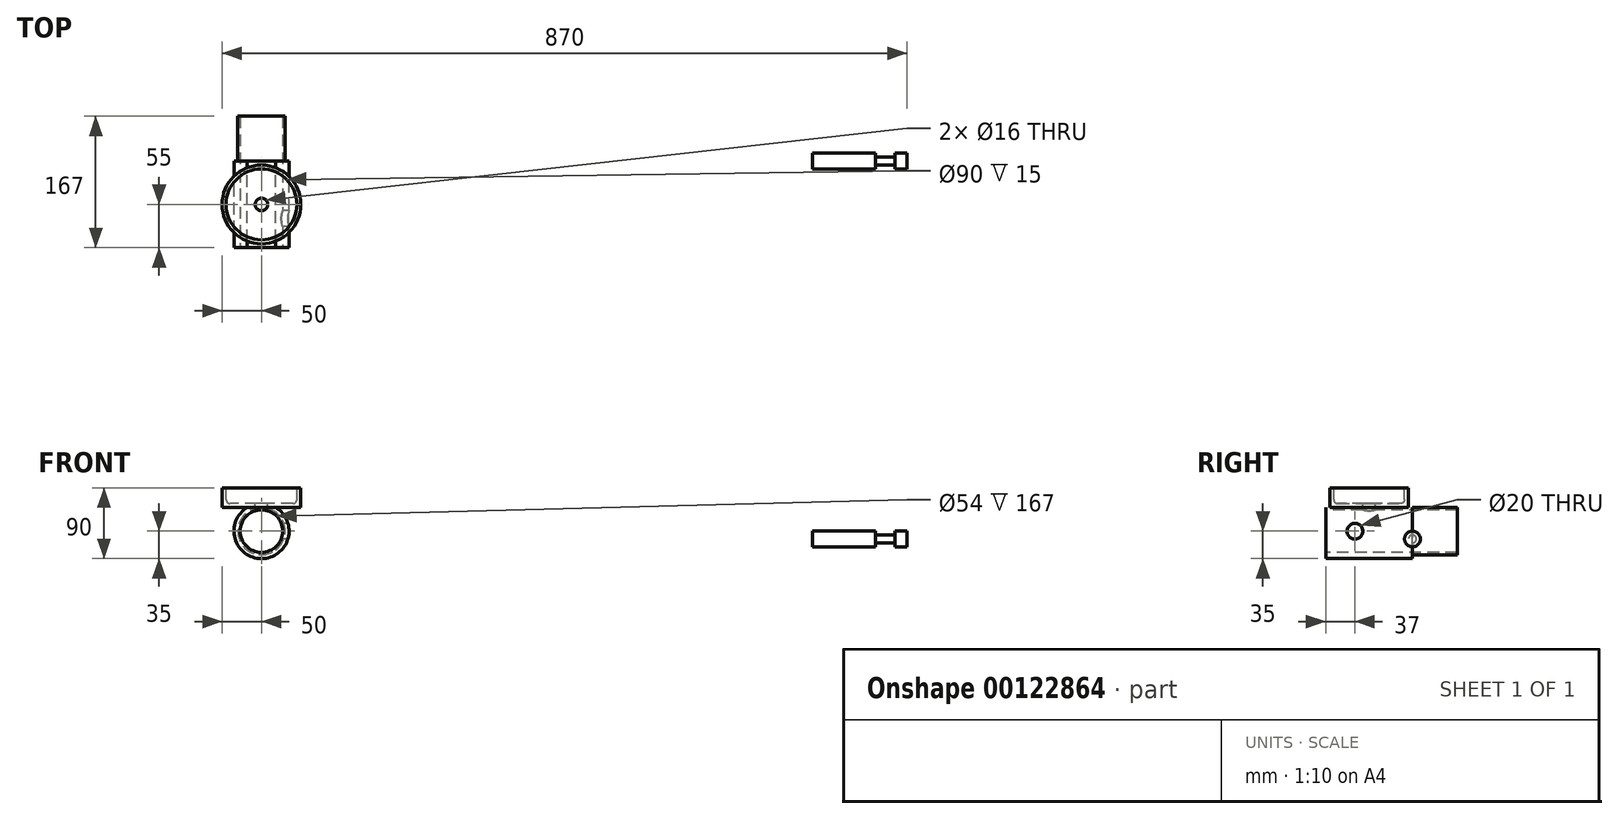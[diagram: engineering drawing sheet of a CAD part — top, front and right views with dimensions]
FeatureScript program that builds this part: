
annotation { "Feature Type Name" : "Feature", "Feature Type Description" : "" }
export const myFeature = defineFeature(function(context is Context, id is Id, definition is map)
    precondition{}
    {
        {
            var Q0;
            Q0=qCreatedBy(makeId("Front.planeOp"),FACE);
            var sketch = newSketch(context, id + "F0", { "sketchPlane" : qUnion([Q0])});
            skArc(sketch, "E0", {"start": v(-16.66, -30.78) * mm, "mid": v(35, 0) * mm, "end": v(-16.66, 30.78) * mm});
            skArc(sketch, "E1", {"start": v(-618.13, 87.33) * mm, "mid": v(-673.03, 71.59) * mm, "end": v(-640, 25) * mm});
            skCircle(sketch, "E2", {"center": v(-700, 0) * mm, "radius": 27.5 * mm, "construction": true});
            skCircle(sketch, "E3", {"center": v(-640, 60) * mm, "radius": 26.5 * mm});
            skCircle(sketch, "E4", {"center": v(-640, -60) * mm, "radius": 26.5 * mm});
            skCircle(sketch, "E5", {"center": v(0, 0) * mm, "radius": 26.5 * mm});
            skLineSegment(sketch, "E6", {"start": v(-40.48, 24.76) * mm, "end": v(-475.65, 24.99) * mm});
            skLineSegment(sketch, "E7", {"start": v(-40.48, -24.76) * mm, "end": v(-475.65, -24.99) * mm});
            skLineSegment(sketch, "E8", {"start": v(-521.62, -36.2) * mm, "end": v(-609.9, -81.98) * mm});
            skLineSegment(sketch, "E9", {"start": v(-521.62, 36.2) * mm, "end": v(-609.9, 81.98) * mm});
            skPoint(sketch, "E10.visualSharp", {"position": v(-500, 25) * mm});
            skArc(sketch, "E10.filletArc", {"start": v(-521.62, 36.2) * mm, "mid": v(-499.3, 27.84) * mm, "end": v(-475.65, 24.99) * mm});
            skPoint(sketch, "E11.visualSharp", {"position": v(-500, -25) * mm});
            skArc(sketch, "E11.filletArc", {"start": v(-475.65, -24.99) * mm, "mid": v(-499.3, -27.84) * mm, "end": v(-521.62, -36.2) * mm});
            skPoint(sketch, "E12.visualSharp", {"position": v(-615.25, 84.75) * mm});
            skArc(sketch, "E13", {"start": v(-640, -25) * mm, "mid": v(-673.03, -71.59) * mm, "end": v(-618.13, -87.33) * mm});
            skFitSpline(sketch, "E14", {"points": [v(-640, -25) * mm, v(-580, 0) * mm, v(-640, 25) * mm], "startDerivative": vector(150, -30) * mm, "endDerivative": vector(-150, -30) * mm});
            skPoint(sketch, "E15.visualSharp", {"position": v(-615.25, -84.75) * mm});
            skLineSegment(sketch, "E16", {"start": v(-24.75, 24.75) * mm, "end": v(0, 0) * mm, "construction": true});
            skLineSegment(sketch, "E17", {"start": v(-24.75, -24.75) * mm, "end": v(0, 0) * mm, "construction": true});
            skPoint(sketch, "E18.visualSharp", {"position": v(-24.75, 24.75) * mm});
            skArc(sketch, "E18.filletArc", {"start": v(-40.48, 24.76) * mm, "mid": v(-28.2, 26.28) * mm, "end": v(-16.66, 30.78) * mm});
            skPoint(sketch, "E19.visualSharp", {"position": v(-24.75, -24.75) * mm});
            skArc(sketch, "E19.filletArc", {"start": v(-16.66, -30.78) * mm, "mid": v(-28.2, -26.28) * mm, "end": v(-40.48, -24.76) * mm});
            skLineSegment(sketch, "E20", {"start": v(-615.25, 84.75) * mm, "end": v(-640, 60) * mm, "construction": true});
            skLineSegment(sketch, "E21", {"start": v(-640, -60) * mm, "end": v(-640, 177.49) * mm, "construction": true});
            skArc(sketch, "E22.filletArc", {"start": v(-618.13, 87.33) * mm, "mid": v(-614.15, 84.45) * mm, "end": v(-609.9, 81.98) * mm});
            skLineSegment(sketch, "E23", {"start": v(-615.25, -84.75) * mm, "end": v(-640, -60) * mm, "construction": true});
            skArc(sketch, "E24.filletArc", {"start": v(-609.9, -81.98) * mm, "mid": v(-614.15, -84.45) * mm, "end": v(-618.13, -87.33) * mm});
            skSolve(sketch);
        }
        {
            var Q0;
            Q0=qSketchRegion(id+"F0",true);
            extrude(context, id + "F1", {"entities" : qUnion([Q0]), "depth" : 45 * mm});
        }
        {
            var Q0;
            Q0=makeQuery(id+"F1.opExtrude","SWEPT_BODY",BODY,{"disambiguationData":[OSD([sQuery(id+"F0.wireOp",EDGE,"E0"),sQuery(id+"F0.wireOp",EDGE,"E1"),sQuery(id+"F0.wireOp",EDGE,"hKVllitM-rUlu-PjKN-B9u5-COeOs3Kio4uB"),sQuery(id+"F0.wireOp",EDGE,"bIEpRebq-8nbQ-7rQF-Jdrm-i3E8cfRsBNN9"),sQuery(id+"F0.wireOp",EDGE,"ymSRshFr-buK2-GFJu-27zL-H9ECYoIg19t0"),sQuery(id+"F0.wireOp",EDGE,"e6450e41-44a2-4cb5-af14-4686bec827bc"),sQuery(id+"F0.wireOp",EDGE,"ipdW7DlG-pZfv-p4Vr-qYAQ-uRQYnpMPVyQN"),sQuery(id+"F0.wireOp",EDGE,"9qNpO7d9-6r7V-397W-DIXA-CVevZtzhY8f4"),sQuery(id+"F0.wireOp",EDGE,"E3"),sQuery(id+"F0.wireOp",EDGE,"E4"),sQuery(id+"F0.wireOp",EDGE,"E5")])]});
            var Q1;
            Q1=makeQuery(id+"F1.opExtrude","CAP_EDGE",EDGE,{"disambiguationData":[OSD([sQuery(id+"F0.wireOp",EDGE,"E5")])],"isStart":false});
            transform(context, id + "F2", {"entities" : qUnion([Q0]), "transformType" : TransformType.ROTATION, "transformAxis" : qUnion([Q1]), "angle" : 12.5 * degree, "makeCopy" : true});
        }
        {
            var Q0;
            Q0=makeQuery(id+"F1.opExtrude","CAP_FACE",FACE,{"disambiguationData":[OSD([sQuery(id+"F0.wireOp",EDGE,"E0"),sQuery(id+"F0.wireOp",EDGE,"E1"),sQuery(id+"F0.wireOp",EDGE,"E3"),sQuery(id+"F0.wireOp",EDGE,"E4"),sQuery(id+"F0.wireOp",EDGE,"E5"),sQuery(id+"F0.wireOp",EDGE,"E6"),sQuery(id+"F0.wireOp",EDGE,"E7"),sQuery(id+"F0.wireOp",EDGE,"E8"),sQuery(id+"F0.wireOp",EDGE,"E9"),sQuery(id+"F0.wireOp",EDGE,"E10.filletArc"),sQuery(id+"F0.wireOp",EDGE,"E11.filletArc"),sQuery(id+"F0.wireOp",EDGE,"E13"),sQuery(id+"F0.wireOp",EDGE,"E14"),sQuery(id+"F0.wireOp",EDGE,"E18.filletArc"),sQuery(id+"F0.wireOp",EDGE,"E19.filletArc"),sQuery(id+"F0.wireOp",EDGE,"E22.filletArc"),sQuery(id+"F0.wireOp",EDGE,"E24.filletArc")])],"isStart":false});
            var sketch = newSketch(context, id + "F3", { "sketchPlane" : qUnion([Q0])});
            skLineSegment(sketch, "E25", {"start": v(-41.5, 14.76) * mm, "end": v(-502.44, 15) * mm});
            skLineSegment(sketch, "E26", {"start": v(-41.5, -14.76) * mm, "end": v(-502.44, -15) * mm});
            skLineSegment(sketch, "E27", {"start": v(-502.44, -15) * mm, "end": v(-592.4, -61.64) * mm});
            skLineSegment(sketch, "E28", {"start": v(-592.4, -61.64) * mm, "end": v(-606.21, -35) * mm});
            skLineSegment(sketch, "E29", {"start": v(-606.21, -35) * mm, "end": v(-564.37, -13.32) * mm});
            skLineSegment(sketch, "E30", {"start": v(-502.44, 15) * mm, "end": v(-592.4, 61.64) * mm});
            skLineSegment(sketch, "E31", {"start": v(-592.4, 61.64) * mm, "end": v(-606.21, 35) * mm});
            skLineSegment(sketch, "E32", {"start": v(-606.21, 35) * mm, "end": v(-564.37, 13.32) * mm});
            skPoint(sketch, "E33.visualSharp", {"position": v(-538.69, 0) * mm});
            skArc(sketch, "E33.filletArc", {"start": v(-564.37, -13.32) * mm, "mid": v(-556.28, 0) * mm, "end": v(-564.37, 13.32) * mm});
            skLineSegment(sketch, "E34", {"start": v(-41.5, 14.76) * mm, "end": v(-41.5, -14.76) * mm});
            skSolve(sketch);
        }
        {
            var Q0;
            Q0=qSketchRegion(id+"F3",true);
            extrude(context, id + "F4", {"entities" : qUnion([Q0]), "operationType" : NewBodyOperationType.REMOVE, "oppositeDirection" : true, "depth" : 17.5 * mm});
        }
        {
            var Q0;
            Q0=makeQuery(id+"F1.opExtrude","CAP_FACE",FACE,{"disambiguationData":[OSD([sQuery(id+"F0.wireOp",EDGE,"E0"),sQuery(id+"F0.wireOp",EDGE,"E1"),sQuery(id+"F0.wireOp",EDGE,"E3"),sQuery(id+"F0.wireOp",EDGE,"E4"),sQuery(id+"F0.wireOp",EDGE,"E5"),sQuery(id+"F0.wireOp",EDGE,"E6"),sQuery(id+"F0.wireOp",EDGE,"E7"),sQuery(id+"F0.wireOp",EDGE,"E8"),sQuery(id+"F0.wireOp",EDGE,"E9"),sQuery(id+"F0.wireOp",EDGE,"E10.filletArc"),sQuery(id+"F0.wireOp",EDGE,"E11.filletArc"),sQuery(id+"F0.wireOp",EDGE,"E13"),sQuery(id+"F0.wireOp",EDGE,"E14"),sQuery(id+"F0.wireOp",EDGE,"E18.filletArc"),sQuery(id+"F0.wireOp",EDGE,"E19.filletArc"),sQuery(id+"F0.wireOp",EDGE,"E22.filletArc"),sQuery(id+"F0.wireOp",EDGE,"E24.filletArc")])],"isStart":true});
            var sketch = newSketch(context, id + "F5", { "sketchPlane" : qUnion([Q0])});
            skLineSegment(sketch, "E35", {"start": v(41.5, 14.76) * mm, "end": v(502.44, 15) * mm});
            skLineSegment(sketch, "E36", {"start": v(502.44, 15) * mm, "end": v(592.4, 61.64) * mm});
            skLineSegment(sketch, "E37", {"start": v(592.4, 61.64) * mm, "end": v(606.21, 35) * mm});
            skLineSegment(sketch, "E38", {"start": v(606.21, -35) * mm, "end": v(592.4, -61.64) * mm});
            skLineSegment(sketch, "E39", {"start": v(592.4, -61.64) * mm, "end": v(502.44, -15) * mm});
            skLineSegment(sketch, "E40", {"start": v(502.44, -15) * mm, "end": v(41.5, -14.76) * mm});
            skLineSegment(sketch, "E41", {"start": v(41.5, 14.76) * mm, "end": v(41.5, -14.76) * mm});
            skLineSegment(sketch, "E42", {"start": v(606.21, 35) * mm, "end": v(564.37, 13.32) * mm});
            skLineSegment(sketch, "E43", {"start": v(564.37, -13.32) * mm, "end": v(606.21, -35) * mm});
            skPoint(sketch, "E44.visualSharp", {"position": v(538.69, 0) * mm});
            skArc(sketch, "E44.filletArc", {"start": v(564.37, 13.32) * mm, "mid": v(556.28, 0) * mm, "end": v(564.37, -13.32) * mm});
            skSolve(sketch);
        }
        {
            var Q0;
            Q0=qSketchRegion(id+"F5",true);
            extrude(context, id + "F6", {"entities" : qUnion([Q0]), "operationType" : NewBodyOperationType.REMOVE, "oppositeDirection" : true, "depth" : 17.5 * mm});
        }
        {
            var Q0;
            Q0=makeQuery(id+"F6.boolean.opBoolean","COPY",EDGE,{"derivedFrom":makeQuery(id+"F6.opExtrude","CAP_EDGE",EDGE,{"disambiguationData":[OSD([sQuery(id+"F5.wireOp",EDGE,"E35")])],"isStart":false})});
            var Q1;
            Q1=makeQuery(id+"F6.boolean.opBoolean","COPY",EDGE,{"derivedFrom":makeQuery(id+"F6.opExtrude","CAP_EDGE",EDGE,{"disambiguationData":[OSD([sQuery(id+"F5.wireOp",EDGE,"E41")])],"isStart":false})});
            var Q2;
            Q2=makeQuery(id+"F6.boolean.opBoolean","COPY",EDGE,{"derivedFrom":makeQuery(id+"F6.opExtrude","CAP_EDGE",EDGE,{"disambiguationData":[OSD([sQuery(id+"F5.wireOp",EDGE,"E40")])],"isStart":false})});
            var Q3;
            Q3=makeQuery(id+"F6.boolean.opBoolean","COPY",EDGE,{"derivedFrom":makeQuery(id+"F6.opExtrude","CAP_EDGE",EDGE,{"disambiguationData":[OSD([sQuery(id+"F5.wireOp",EDGE,"E36")])],"isStart":false})});
            var Q4;
            Q4=makeQuery(id+"F6.boolean.opBoolean","COPY",EDGE,{"derivedFrom":makeQuery(id+"F6.opExtrude","CAP_EDGE",EDGE,{"disambiguationData":[OSD([sQuery(id+"F5.wireOp",EDGE,"E39")])],"isStart":false})});
            var Q5;
            Q5=makeQuery(id+"F6.boolean.opBoolean","COPY",EDGE,{"derivedFrom":makeQuery(id+"F6.opExtrude","CAP_EDGE",EDGE,{"disambiguationData":[OSD([sQuery(id+"F5.wireOp",EDGE,"E38")])],"isStart":false})});
            var Q6;
            Q6=makeQuery(id+"F6.boolean.opBoolean","COPY",EDGE,{"derivedFrom":makeQuery(id+"F6.opExtrude","CAP_EDGE",EDGE,{"disambiguationData":[OSD([sQuery(id+"F5.wireOp",EDGE,"E43")])],"isStart":false})});
            var Q7;
            Q7=makeQuery(id+"F6.boolean.opBoolean","COPY",EDGE,{"derivedFrom":makeQuery(id+"F6.opExtrude","CAP_EDGE",EDGE,{"disambiguationData":[OSD([sQuery(id+"F5.wireOp",EDGE,"E37")])],"isStart":false})});
            fillet(context, id + "F7", {"entities" : qUnion([Q0, Q1, Q2, Q3, Q4, Q5, Q6, Q7]), "radius" : 5 * mm, "tangentPropagation" : true, "allowEdgeOverflow" : false});
        }
        {
            var Q0;
            Q0=makeQuery(id+"F4.boolean.opBoolean","COPY",EDGE,{"derivedFrom":makeQuery(id+"F4.opExtrude","CAP_EDGE",EDGE,{"disambiguationData":[OSD([sQuery(id+"F3.wireOp",EDGE,"E28")])],"isStart":false})});
            var Q1;
            Q1=makeQuery(id+"F4.boolean.opBoolean","COPY",EDGE,{"derivedFrom":makeQuery(id+"F4.opExtrude","CAP_EDGE",EDGE,{"disambiguationData":[OSD([sQuery(id+"F3.wireOp",EDGE,"E27")])],"isStart":false})});
            var Q2;
            Q2=makeQuery(id+"F4.boolean.opBoolean","COPY",EDGE,{"derivedFrom":makeQuery(id+"F4.opExtrude","CAP_EDGE",EDGE,{"disambiguationData":[OSD([sQuery(id+"F3.wireOp",EDGE,"E26")])],"isStart":false})});
            var Q3;
            Q3=makeQuery(id+"F4.boolean.opBoolean","COPY",EDGE,{"derivedFrom":makeQuery(id+"F4.opExtrude","CAP_EDGE",EDGE,{"disambiguationData":[OSD([sQuery(id+"F3.wireOp",EDGE,"E32")])],"isStart":false})});
            var Q4;
            Q4=makeQuery(id+"F4.boolean.opBoolean","COPY",EDGE,{"derivedFrom":makeQuery(id+"F4.opExtrude","CAP_EDGE",EDGE,{"disambiguationData":[OSD([sQuery(id+"F3.wireOp",EDGE,"E31")])],"isStart":false})});
            var Q5;
            Q5=makeQuery(id+"F4.boolean.opBoolean","COPY",EDGE,{"derivedFrom":makeQuery(id+"F4.opExtrude","CAP_EDGE",EDGE,{"disambiguationData":[OSD([sQuery(id+"F3.wireOp",EDGE,"E30")])],"isStart":false})});
            var Q6;
            Q6=makeQuery(id+"F4.boolean.opBoolean","COPY",EDGE,{"derivedFrom":makeQuery(id+"F4.opExtrude","CAP_EDGE",EDGE,{"disambiguationData":[OSD([sQuery(id+"F3.wireOp",EDGE,"E25")])],"isStart":false})});
            var Q7;
            Q7=makeQuery(id+"F4.boolean.opBoolean","COPY",EDGE,{"derivedFrom":makeQuery(id+"F4.opExtrude","CAP_EDGE",EDGE,{"disambiguationData":[OSD([sQuery(id+"F3.wireOp",EDGE,"E34")])],"isStart":false})});
            fillet(context, id + "F8", {"entities" : qUnion([Q0, Q1, Q2, Q3, Q4, Q5, Q6, Q7]), "radius" : 5 * mm, "tangentPropagation" : true, "allowEdgeOverflow" : false});
        }
        {
            var Q0;
            Q0=qCreatedBy(makeId("Front.planeOp"),FACE);
            var sketch = newSketch(context, id + "F9", { "sketchPlane" : qUnion([Q0])});
            skArc(sketch, "E45", {"start": v(-700, -43.5) * mm, "mid": v(-656.5, 0) * mm, "end": v(-700, 43.5) * mm});
            skCircle(sketch, "E46", {"center": v(0, 0) * mm, "radius": 642.8 * mm, "construction": true});
            skPoint(sketch, "E47", {"position": v(-640, 60) * mm});
            skPoint(sketch, "E48", {"position": v(-640, -60) * mm});
            skCircle(sketch, "E49", {"center": v(-640, 60) * mm, "radius": 7.5 * mm});
            skCircle(sketch, "E50", {"center": v(-640, -60) * mm, "radius": 7.5 * mm});
            skArc(sketch, "E51", {"start": v(-626.73, 53) * mm, "mid": v(-629.42, 70.63) * mm, "end": v(-647.06, 73.24) * mm});
            skArc(sketch, "E52", {"start": v(-647.06, -73.24) * mm, "mid": v(-629.42, -70.63) * mm, "end": v(-626.73, -53) * mm});
            skLineSegment(sketch, "E53", {"start": v(-700, 45) * mm, "end": v(-647.06, 73.24) * mm});
            skLineSegment(sketch, "E54", {"start": v(-642.38, 23.32) * mm, "end": v(-626.73, 53) * mm});
            skLineSegment(sketch, "E55", {"start": v(-647.06, -73.24) * mm, "end": v(-700, -45) * mm});
            skLineSegment(sketch, "E56", {"start": v(-626.73, -53) * mm, "end": v(-642.38, -23.32) * mm});
            skPoint(sketch, "E57.visualSharp", {"position": v(-654.68, 0) * mm});
            skArc(sketch, "E57.filletArc", {"start": v(-642.38, 23.32) * mm, "mid": v(-648.16, 0) * mm, "end": v(-642.38, -23.32) * mm});
            skLineSegment(sketch, "E58", {"start": v(-700, -91.27) * mm, "end": v(-700, 112.6) * mm, "construction": true});
            skArc(sketch, "E59", {"start": v(-691.4, -48.75) * mm, "mid": v(-650.5, 0) * mm, "end": v(-691.4, 48.75) * mm});
            skArc(sketch, "E60", {"start": v(-692.1, -44.8) * mm, "mid": v(-654.5, 0) * mm, "end": v(-692.1, 44.8) * mm});
            skLineSegment(sketch, "E61", {"start": v(-700, 45) * mm, "end": v(-700, 43.5) * mm});
            skLineSegment(sketch, "E62", {"start": v(-700, -45) * mm, "end": v(-700, -43.5) * mm});
            skLineSegment(sketch, "E63", {"start": v(-700, 0) * mm, "end": v(-690.13, 55.95) * mm, "construction": true});
            skLineSegment(sketch, "E64", {"start": v(-700, 0) * mm, "end": v(-689.73, -58.24) * mm, "construction": true});
            skLineSegment(sketch, "E65", {"start": v(-692.1, -44.8) * mm, "end": v(-691.4, -48.75) * mm});
            skLineSegment(sketch, "E66", {"start": v(-691.4, 48.75) * mm, "end": v(-692.1, 44.8) * mm});
            skSolve(sketch);
        }
        {
            var Q0;
            Q0=qSketchRegion(id+"F9",true);
            extrude(context, id + "F10", {"entities" : qUnion([Q0]), "oppositeDirection" : true, "depth" : 5 * mm});
        }
        {
            var Q0;
            Q0=makeQuery(id+"F2.opPattern","COPY",BODY,{"derivedFrom":makeQuery(id+"F1.opExtrude","SWEPT_BODY",BODY,{"disambiguationData":[OSD([sQuery(id+"F0.wireOp",EDGE,"E0"),sQuery(id+"F0.wireOp",EDGE,"E1"),sQuery(id+"F0.wireOp",EDGE,"E3"),sQuery(id+"F0.wireOp",EDGE,"E4"),sQuery(id+"F0.wireOp",EDGE,"E5"),sQuery(id+"F0.wireOp",EDGE,"E6"),sQuery(id+"F0.wireOp",EDGE,"E7"),sQuery(id+"F0.wireOp",EDGE,"E8"),sQuery(id+"F0.wireOp",EDGE,"E9"),sQuery(id+"F0.wireOp",EDGE,"E10.filletArc"),sQuery(id+"F0.wireOp",EDGE,"E11.filletArc"),sQuery(id+"F0.wireOp",EDGE,"E13"),sQuery(id+"F0.wireOp",EDGE,"E14"),sQuery(id+"F0.wireOp",EDGE,"E18.filletArc"),sQuery(id+"F0.wireOp",EDGE,"E19.filletArc"),sQuery(id+"F0.wireOp",EDGE,"E22.filletArc"),sQuery(id+"F0.wireOp",EDGE,"E24.filletArc")])]}),"instanceName":"1"});
            deleteBodies(context, id + "F11", {"entities" : qUnion([Q0])});
        }
        {
            var Q0;
            Q0=makeQuery(id+"F1.opExtrude","SWEPT_BODY",BODY,{"disambiguationData":[OSD([sQuery(id+"F0.wireOp",EDGE,"E0"),sQuery(id+"F0.wireOp",EDGE,"E1"),sQuery(id+"F0.wireOp",EDGE,"E3"),sQuery(id+"F0.wireOp",EDGE,"E4"),sQuery(id+"F0.wireOp",EDGE,"E5"),sQuery(id+"F0.wireOp",EDGE,"E6"),sQuery(id+"F0.wireOp",EDGE,"E7"),sQuery(id+"F0.wireOp",EDGE,"E8"),sQuery(id+"F0.wireOp",EDGE,"E9"),sQuery(id+"F0.wireOp",EDGE,"E10.filletArc"),sQuery(id+"F0.wireOp",EDGE,"E11.filletArc"),sQuery(id+"F0.wireOp",EDGE,"E13"),sQuery(id+"F0.wireOp",EDGE,"E14"),sQuery(id+"F0.wireOp",EDGE,"E18.filletArc"),sQuery(id+"F0.wireOp",EDGE,"E19.filletArc"),sQuery(id+"F0.wireOp",EDGE,"E22.filletArc"),sQuery(id+"F0.wireOp",EDGE,"E24.filletArc")])]});
            deleteBodies(context, id + "F12", {"entities" : qUnion([Q0])});
        }
        {
            var Q0;
            Q0=makeQuery(id+"F10.opExtrude","CAP_FACE",FACE,{"disambiguationData":[OSD([sQuery(id+"F9.wireOp",EDGE,"E45"),sQuery(id+"F9.wireOp",EDGE,"3yjohgCL-tuzw-ZYgi-CheZ-hkjVQce5UM2D"),sQuery(id+"F9.wireOp",EDGE,"E49"),sQuery(id+"F9.wireOp",EDGE,"E50"),sQuery(id+"F9.wireOp",EDGE,"E51"),sQuery(id+"F9.wireOp",EDGE,"E52"),sQuery(id+"F9.wireOp",EDGE,"E53"),sQuery(id+"F9.wireOp",EDGE,"E54"),sQuery(id+"F9.wireOp",EDGE,"E55"),sQuery(id+"F9.wireOp",EDGE,"E56"),sQuery(id+"F9.wireOp",EDGE,"E57.filletArc")])],"isStart":true});
            var sketch = newSketch(context, id + "F13", { "sketchPlane" : qUnion([Q0])});
            skCircle(sketch, "E67", {"center": v(-700, 0) * mm, "radius": 27 * mm});
            skCircle(sketch, "E68", {"center": v(-700, 0) * mm, "radius": 30 * mm});
            skSolve(sketch);
        }
        {
            var Q0;
            Q0=qSketchRegion(id+"F13",true);
            extrude(context, id + "F14", {"entities" : qUnion([Q0]), "oppositeDirection" : true, "depth" : 4 * mm});
        }
        {
            var Q0;
            Q0=makeQuery(id+"F10.opExtrude","CAP_FACE",FACE,{"disambiguationData":[OSD([sQuery(id+"F9.wireOp",EDGE,"E45"),sQuery(id+"F9.wireOp",EDGE,"3yjohgCL-tuzw-ZYgi-CheZ-hkjVQce5UM2D"),sQuery(id+"F9.wireOp",EDGE,"E49"),sQuery(id+"F9.wireOp",EDGE,"E50"),sQuery(id+"F9.wireOp",EDGE,"E51"),sQuery(id+"F9.wireOp",EDGE,"E52"),sQuery(id+"F9.wireOp",EDGE,"E53"),sQuery(id+"F9.wireOp",EDGE,"E54"),sQuery(id+"F9.wireOp",EDGE,"E55"),sQuery(id+"F9.wireOp",EDGE,"E56"),sQuery(id+"F9.wireOp",EDGE,"E57.filletArc")])],"isStart":true});
            var sketch = newSketch(context, id + "F15", { "sketchPlane" : qUnion([Q0])});
            skCircle(sketch, "E69", {"center": v(-700, 0) * mm, "radius": 35 * mm});
            skCircle(sketch, "E70", {"center": v(-700, 0) * mm, "radius": 27 * mm});
            skSolve(sketch);
        }
        {
            var Q0;
            Q0=qSketchRegion(id+"F15",true);
            extrude(context, id + "F16", {"entities" : qUnion([Q0]), "operationType" : NewBodyOperationType.ADD, "depth" : 110 * mm});
        }
        {
            var Q0;
            Q0=makeQuery(id+"F16.opExtrude","CAP_FACE",FACE,{"disambiguationData":[OSD([sQuery(id+"F15.wireOp",EDGE,"E69"),sQuery(id+"F15.wireOp",EDGE,"E70")])],"isStart":false});
            var sketch = newSketch(context, id + "F17", { "sketchPlane" : qUnion([Q0])});
            skLineSegment(sketch, "E71.bottom", {"start": v(-732, 36) * mm, "end": v(-668, 36) * mm});
            skLineSegment(sketch, "E71.top", {"start": v(-732, 30) * mm, "end": v(-668, 30) * mm});
            skLineSegment(sketch, "E71.left", {"start": v(-732, 36) * mm, "end": v(-732, 30) * mm});
            skLineSegment(sketch, "E71.right", {"start": v(-668, 36) * mm, "end": v(-668, 30) * mm});
            skCircle(sketch, "E72", {"center": v(-700, 0) * mm, "radius": 27 * mm, "construction": true});
            skLineSegment(sketch, "E73", {"start": v(-700, 0) * mm, "end": v(-700, 30) * mm, "construction": true});
            skSolve(sketch);
        }
        {
            var Q0;
            Q0=qSketchRegion(id+"F17",true);
            extrude(context, id + "F18", {"entities" : qUnion([Q0]), "operationType" : NewBodyOperationType.REMOVE, "oppositeDirection" : true, "depth" : 110 * mm});
        }
        {
            var Q0;
            Q0=makeQuery(id+"F18.boolean.opBoolean","COPY",FACE,{"derivedFrom":makeQuery(id+"F18.opExtrude","SWEPT_FACE",FACE,{"disambiguationData":[OSD([sQuery(id+"F17.wireOp",EDGE,"E71.top")])]})});
            var sketch = newSketch(context, id + "F19", { "sketchPlane" : qUnion([Q0])});
            skLineSegment(sketch, "E74", {"start": v(-718.03, -55) * mm, "end": v(-681.97, -55) * mm, "construction": true});
            skLineSegment(sketch, "E75", {"start": v(-700, 0) * mm, "end": v(-700, -110) * mm, "construction": true});
            skCircle(sketch, "E76", {"center": v(-700, -55) * mm, "radius": 50 * mm});
            skSolve(sketch);
        }
        {
            var Q0;
            Q0=qSketchRegion(id+"F19",true);
            extrude(context, id + "F20", {"entities" : qUnion([Q0]), "depth" : 25 * mm});
        }
        {
            var Q0;
            Q0=makeQuery(id+"F20.opExtrude","CAP_FACE",FACE,{"disambiguationData":[OSD([sQuery(id+"F19.wireOp",EDGE,"E76")])],"isStart":false});
            var sketch = newSketch(context, id + "F21", { "sketchPlane" : qUnion([Q0])});
            skCircle(sketch, "E77", {"center": v(-700, -55) * mm, "radius": 45 * mm});
            skSolve(sketch);
        }
        {
            var Q0;
            Q0=qSketchRegion(id+"F21",true);
            extrude(context, id + "F22", {"entities" : qUnion([Q0]), "operationType" : NewBodyOperationType.REMOVE, "oppositeDirection" : true, "depth" : 20 * mm});
        }
        {
            var Q0;
            Q0=makeQuery(id+"F22.boolean.opBoolean","COPY",EDGE,{"derivedFrom":makeQuery(id+"F22.opExtrude","CAP_EDGE",EDGE,{"disambiguationData":[OSD([sQuery(id+"F21.wireOp",EDGE,"E77")])],"isStart":false})});
            fillet(context, id + "F23", {"entities" : qUnion([Q0]), "radius" : 5 * mm, "tangentPropagation" : true, "allowEdgeOverflow" : false});
        }
        {
            var Q0;
            Q0=makeQuery(id+"F22.boolean.opBoolean","COPY",FACE,{"derivedFrom":makeQuery(id+"F22.opExtrude","CAP_FACE",FACE,{"disambiguationData":[OSD([sQuery(id+"F21.wireOp",EDGE,"E77")])],"isStart":false})});
            var sketch = newSketch(context, id + "F24", { "sketchPlane" : qUnion([Q0])});
            skCircle(sketch, "E78", {"center": v(-700, -55) * mm, "radius": 8 * mm});
            skLineSegment(sketch, "E79", {"start": v(-700, -55) * mm, "end": v(0, -55) * mm, "construction": true});
            skSolve(sketch);
        }
        {
            var Q0;
            Q0 = qSketchRegion(id + "F24", true);
            var Q1;
            Q1=sQuery(id+"F24.wireOp",EDGE,"E78");
            extrude(context, id + "F25", {"entities" : qUnion([Q0]), "operationType" : NewBodyOperationType.REMOVE, "surfaceEntities" : qUnion([Q1]), "oppositeDirection" : true, "depth" : 10 * mm});
        }
        {
            var Q0;
            Q0=makeQuery(id+"F10.opExtrude","CAP_FACE",FACE,{"disambiguationData":[OSD([sQuery(id+"F9.wireOp",EDGE,"E45"),sQuery(id+"F9.wireOp",EDGE,"3yjohgCL-tuzw-ZYgi-CheZ-hkjVQce5UM2D"),sQuery(id+"F9.wireOp",EDGE,"E49"),sQuery(id+"F9.wireOp",EDGE,"E50"),sQuery(id+"F9.wireOp",EDGE,"E51"),sQuery(id+"F9.wireOp",EDGE,"E52"),sQuery(id+"F9.wireOp",EDGE,"E53"),sQuery(id+"F9.wireOp",EDGE,"E54"),sQuery(id+"F9.wireOp",EDGE,"E55"),sQuery(id+"F9.wireOp",EDGE,"E56"),sQuery(id+"F9.wireOp",EDGE,"E57.filletArc")])],"isStart":false});
            var sketch = newSketch(context, id + "F26", { "sketchPlane" : qUnion([Q0])});
            skCircle(sketch, "E80", {"center": v(700, 0) * mm, "radius": 31.5 * mm});
            skLineSegment(sketch, "E81", {"start": v(700, 31.5) * mm, "end": v(700, -31.5) * mm});
            skCircle(sketch, "E82", {"center": v(700, 0) * mm, "radius": 30.5 * mm});
            skSolve(sketch);
        }
        {
            var Q0;
            {var subQ0=sQuery(id+"F26.wireOp",EDGE,"E81");var subQ1=sQuery(id+"F26.wireOp",EDGE,"E80");var subQ2=makeQuery(id+"F26.imprint","INTERSECT",VERTEX,{"disambiguationData":[OD(0.0)],"derivedFrom":[subQ1,subQ0]});Q0=makeQuery(id+"F26.imprint","IMPRINT",FACE,{"disambiguationData":[TD([[makeQuery(id+"F26.imprint","IMPRINT",EDGE,{"disambiguationData":[TD([[subQ2,-1.0]])],"derivedFrom":subQ1}),1.0]])]});}
            extrude(context, id + "F27", {"entities" : qUnion([Q0]), "operationType" : NewBodyOperationType.REMOVE, "oppositeDirection" : true, "depth" : 4 * mm});
        }
        {
            var Q0;
            Q0=makeQuery(id+"F14.opExtrude","CAP_FACE",FACE,{"disambiguationData":[OSD([sQuery(id+"F13.wireOp",EDGE,"E67"),sQuery(id+"F13.wireOp",EDGE,"E68")])],"isStart":false});
            extrude(context, id + "F28", {"entities" : qUnion([Q0]), "operationType" : NewBodyOperationType.ADD, "depth" : 53 * mm});
        }
        {
            var Q0;
            Q0=qCreatedBy(makeId("Right.planeOp"),FACE);
            cPlane(context, id + "F29", {"entities" : qUnion([Q0]), "cplaneType" : CPlaneType.OFFSET, "offset" : 700 * mm, "oppositeDirection" : true, "width" : 150 * mm, "height" : 150 * mm});
        }
        {
            var Q0;
            Q0=qCreatedBy(id+"F29.planeOp",FACE);
            var sketch = newSketch(context, id + "F30", { "sketchPlane" : qUnion([Q0])});
            skLineSegment(sketch, "E83.0", {"start": v(-110, 30) * mm, "end": v(-110, -35) * mm, "construction": true});
            skLineSegment(sketch, "E84", {"start": v(-110, 0) * mm, "end": v(-73, 0) * mm, "construction": true});
            skPoint(sketch, "E84.startSnap0", {"position": v(-110, -2.5) * mm});
            skCircle(sketch, "E85", {"center": v(-73, 0) * mm, "radius": 10 * mm});
            skSolve(sketch);
        }
        {
            var Q0;
            Q0 = qSketchRegion(id + "F30", true);
            extrude(context, id + "F31", {"entities" : qUnion([Q0]), "operationType" : NewBodyOperationType.REMOVE, "depth" : 50 * mm});
        }
        {
            var Q0;
            Q0=qCreatedBy(makeId("Front.planeOp"),FACE);
            var sketch = newSketch(context, id + "F32", { "sketchPlane" : qUnion([Q0])});
            skLineSegment(sketch, "E86", {"start": v(0, 0) * mm, "end": v(80, 0) * mm});
            skLineSegment(sketch, "E87", {"start": v(80, 0) * mm, "end": v(80, -5) * mm});
            skLineSegment(sketch, "E88", {"start": v(80, -5) * mm, "end": v(105, -5) * mm});
            skLineSegment(sketch, "E89", {"start": v(105, -5) * mm, "end": v(105, 0) * mm});
            skLineSegment(sketch, "E90", {"start": v(105, 0) * mm, "end": v(120, 0) * mm});
            skLineSegment(sketch, "E91", {"start": v(120, 0) * mm, "end": v(120, -10) * mm});
            skLineSegment(sketch, "E92", {"start": v(120, -10) * mm, "end": v(0, -10) * mm});
            skLineSegment(sketch, "E93", {"start": v(0, -10) * mm, "end": v(0, 0) * mm});
            skSolve(sketch);
        }
        {
            var Q0;
            Q0=makeQuery(id+"F32.imprint","IMPRINT",FACE,{"disambiguationData":[TD([[makeQuery(id+"F32.imprint","IMPRINT",EDGE,{"derivedFrom":sQuery(id+"F32.wireOp",EDGE,"E86")}),-1.0]])]});
            var Q1;
            Q1=sQuery(id+"F32.wireOp",EDGE,"E92");
            revolve(context, id + "F33", {"entities" : qUnion([Q0]), "axis" : qUnion([Q1]), "revolveType" : RevolveType.FULL});
        }
        {
            var Q0;
            Q0=makeQuery(id+"F27.boolean.opBoolean","SPLIT",BODY,{"disambiguationData":[OD(0.0)],"derivedFrom":makeQuery(id+"F10.opExtrude","SWEPT_BODY",BODY,{"disambiguationData":[OSD([sQuery(id+"F9.wireOp",EDGE,"E45"),sQuery(id+"F9.wireOp",EDGE,"E49"),sQuery(id+"F9.wireOp",EDGE,"E50"),sQuery(id+"F9.wireOp",EDGE,"E51"),sQuery(id+"F9.wireOp",EDGE,"E52"),sQuery(id+"F9.wireOp",EDGE,"E53"),sQuery(id+"F9.wireOp",EDGE,"E54"),sQuery(id+"F9.wireOp",EDGE,"E55"),sQuery(id+"F9.wireOp",EDGE,"E56"),sQuery(id+"F9.wireOp",EDGE,"E57.filletArc"),sQuery(id+"F9.wireOp",EDGE,"E59"),sQuery(id+"F9.wireOp",EDGE,"E60"),sQuery(id+"F9.wireOp",EDGE,"E61"),sQuery(id+"F9.wireOp",EDGE,"E62"),sQuery(id+"F9.wireOp",EDGE,"E65"),sQuery(id+"F9.wireOp",EDGE,"E66")])]})});
            deleteBodies(context, id + "F34", {"entities" : qUnion([Q0])});
        }
    });
